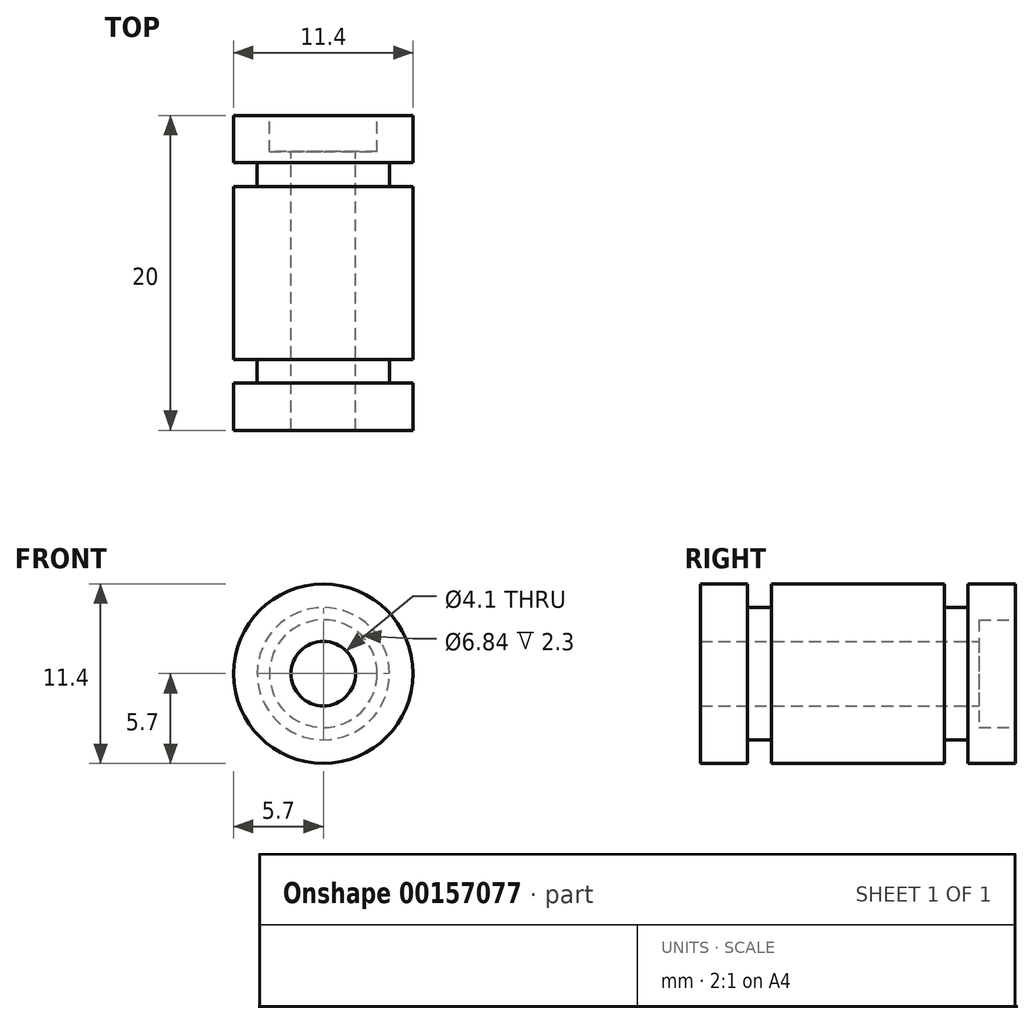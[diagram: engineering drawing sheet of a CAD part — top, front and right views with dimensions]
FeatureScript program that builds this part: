
annotation { "Feature Type Name" : "Feature", "Feature Type Description" : "" }
export const myFeature = defineFeature(function(context is Context, id is Id, definition is map)
    precondition{}
    {
        {
            var Q0;
            Q0=qCreatedBy(makeId("Right.planeOp"),FACE);
            var sketch = newSketch(context, id + "F0", { "sketchPlane" : qUnion([Q0])});
            skLineSegment(sketch, "E0", {"start": v(11.47, 0) * mm, "end": v(0, 0) * mm, "construction": true});
            skLineSegment(sketch, "E1", {"start": v(17.7, 2.05) * mm, "end": v(0, 2.05) * mm});
            skLineSegment(sketch, "E2", {"start": v(17.7, 2.05) * mm, "end": v(17.7, 3.42) * mm});
            skLineSegment(sketch, "E3", {"start": v(20, 3.42) * mm, "end": v(17.7, 3.42) * mm});
            skLineSegment(sketch, "E4", {"start": v(20, 3.42) * mm, "end": v(20, 5.7) * mm});
            skLineSegment(sketch, "E5", {"start": v(17, 5.7) * mm, "end": v(20, 5.7) * mm});
            skLineSegment(sketch, "E6", {"start": v(17, 5.7) * mm, "end": v(17, 4.2) * mm});
            skLineSegment(sketch, "E7", {"start": v(15.5, 4.2) * mm, "end": v(17, 4.2) * mm});
            skLineSegment(sketch, "E8", {"start": v(3, 4.2) * mm, "end": v(3, 5.7) * mm});
            skLineSegment(sketch, "E9", {"start": v(0, 5.7) * mm, "end": v(3, 5.7) * mm});
            skLineSegment(sketch, "E10", {"start": v(0, 5.7) * mm, "end": v(0, 2.05) * mm});
            skLineSegment(sketch, "E11", {"start": v(4.5, 4.2) * mm, "end": v(4.5, 5.7) * mm});
            skLineSegment(sketch, "E12", {"start": v(4.5, 5.7) * mm, "end": v(15.5, 5.7) * mm});
            skLineSegment(sketch, "E13", {"start": v(15.5, 5.7) * mm, "end": v(15.5, 4.2) * mm});
            skLineSegment(sketch, "E14.trimOffspring", {"start": v(4.5, 4.2) * mm, "end": v(3, 4.2) * mm});
            skSolve(sketch);
        }
        {
            var Q0;
            Q0=makeQuery(id+"F0.imprint","IMPRINT",FACE,{"disambiguationData":[TD([[makeQuery(id+"F0.imprint","IMPRINT",EDGE,{"derivedFrom":sQuery(id+"F0.wireOp",EDGE,"E1")}),-1.0]])]});
            var Q1;
            Q1=sQuery(id+"F0.wireOp",EDGE,"E0");
            revolve(context, id + "F1", {"entities" : qUnion([Q0]), "axis" : qUnion([Q1]), "revolveType" : RevolveType.FULL});
        }
    });
